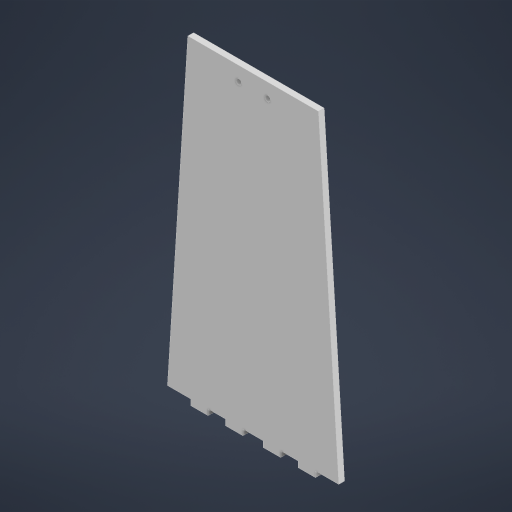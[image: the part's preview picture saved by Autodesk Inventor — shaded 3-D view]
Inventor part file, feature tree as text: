
AUTODESK INVENTOR PART (.ipt)
format: ipt  version: 2023.2 (Build 272271000, 271)  size: 240,128 bytes
history: native  units: mm
features: sketch x2, extrude x1
ambient origin geometry x8: Origin, YZ Plane, XZ Plane, XY Plane, X Axis, Y Axis, Z Axis, Center Point
bodies: Body1 (feature_tree)
feature tree (3):
  extrude  "Extrusion17"  Depth=16.0mm
  sketch  "Sketch1"  dims[d229=90.0mm d232=16.0mm]
  sketch  "Sketch2"  dims[d233=12.0mm d234=12.0mm d235=4.0mm d237=4.0mm d238=0.0mm d239=14.0mm d241=220.0mm d242=4.0mm d244=10.0mm d245=20.0mm d246=4.0mm d247=0.0mm d9=0.5mm d10=0.872665mm d11=0.5mm d12=0.872665mm d13=0.5mm d14=0.872665mm d27=0.5mm d28=0.872665mm d29=0.5mm d30=0.872665mm d88=0.5mm d89=0.872665mm d90=0.5mm d91=0.872665mm d116=0.5mm d117=0.872665mm d118=0.5mm d119=0.872665mm d154=0.5mm d155=0.872665mm d156=0.5mm d157=0.872665mm d181=0.5mm d182=0.872665mm d183=0.5mm d184=0.872665mm d221=0.5mm d222=0.872665mm d223=0.5mm d224=0.872665mm]
